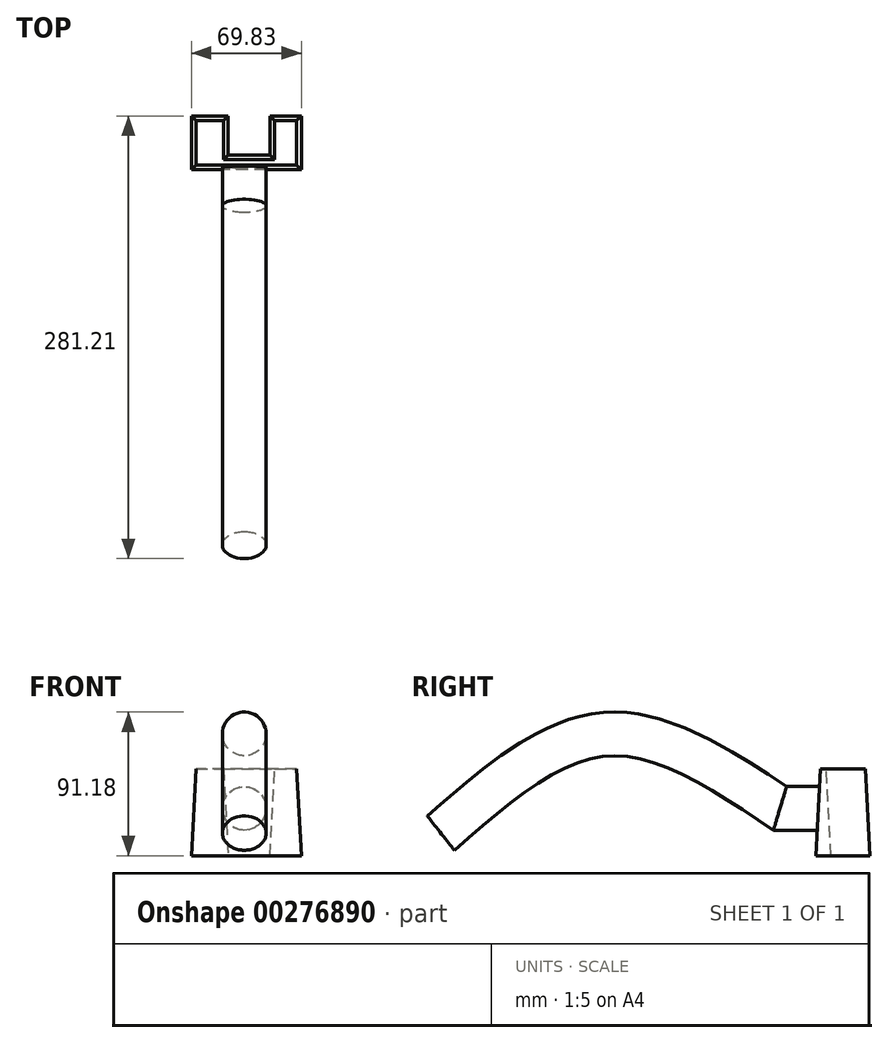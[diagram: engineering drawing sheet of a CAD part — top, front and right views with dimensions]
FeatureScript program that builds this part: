
annotation { "Feature Type Name" : "Feature", "Feature Type Description" : "" }
export const myFeature = defineFeature(function(context is Context, id is Id, definition is map)
    precondition{}
    {
        {
            var Q0;
            Q0=qCreatedBy(makeId("Top.planeOp"),FACE);
            var sketch = newSketch(context, id + "F0", { "sketchPlane" : qUnion([Q0])});
            skLineSegment(sketch, "E0.bottom", {"start": v(0, 0) * mm, "end": v(69.83, 0) * mm});
            skLineSegment(sketch, "E0.top", {"start": v(0, 34.25) * mm, "end": v(23.28, 34.25) * mm});
            skLineSegment(sketch, "E0.left", {"start": v(0, 0) * mm, "end": v(0, 34.25) * mm});
            skLineSegment(sketch, "E0.right", {"start": v(69.83, 0) * mm, "end": v(69.83, 34.25) * mm});
            skLineSegment(sketch, "E1.top", {"start": v(23.28, 9.39) * mm, "end": v(49.99, 9.39) * mm});
            skLineSegment(sketch, "E1.left", {"start": v(23.28, 34.25) * mm, "end": v(23.28, 9.39) * mm});
            skLineSegment(sketch, "E1.right", {"start": v(49.99, 34.25) * mm, "end": v(49.99, 9.39) * mm});
            skLineSegment(sketch, "E2.trimOffspring", {"start": v(49.99, 34.25) * mm, "end": v(69.83, 34.25) * mm});
            skSolve(sketch);
        }
        {
            var Q0;
            Q0=makeQuery(id+"F0.imprint","IMPRINT",FACE,{"disambiguationData":[TD([[makeQuery(id+"F0.imprint","IMPRINT",EDGE,{"derivedFrom":sQuery(id+"F0.wireOp",EDGE,"E0.bottom")}),1.0]])]});
            extrude(context, id + "F1", {"entities" : qUnion([Q0]), "depth" : 55.12 * mm, "hasDraft" : true, "draftAngle" : 3 * degree, "draftPullDirection" : true});
        }
        {
            var Q0;
            Q0=makeQuery(id+"F1.opExtrude","SWEPT_FACE",FACE,{"disambiguationData":[OSD([sQuery(id+"F0.wireOp",EDGE,"E0.bottom")])]});
            var sketch = newSketch(context, id + "F2", { "sketchPlane" : qUnion([Q0])});
            skCircle(sketch, "E3", {"center": v(33.6, 30.06) * mm, "radius": 13.87 * mm});
            skSolve(sketch);
        }
        {
            var Q0;
            Q0=qCreatedBy(makeId("Right.planeOp"),FACE);
            var sketch = newSketch(context, id + "F3", { "sketchPlane" : qUnion([Q0])});
            skLineSegment(sketch, "E4", {"start": v(3.44, 29.76) * mm, "end": v(-23.01, 29.76) * mm});
            skPoint(sketch, "E5.3.internal.orphan", {"position": v(-71.94, 29.76) * mm});
            skFitSpline(sketch, "E6", {"points": [v(-23.01, 29.76) * mm, v(-133.16, 76.9) * mm, v(-238.22, 14.1) * mm], "startDerivative": vector(-224.58, 149.42) * mm, "endDerivative": vector(-205.88, -180.13) * mm});
            skSolve(sketch);
        }
        {
            var Q0;
            Q0=makeQuery(id+"F2.imprint","IMPRINT",FACE,{"disambiguationData":[TD([[makeQuery(id+"F2.imprint","IMPRINT",EDGE,{"derivedFrom":sQuery(id+"F2.wireOp",EDGE,"E3")}),1.0]])]});
            var Q1;
            Q1=sQuery(id+"F3.wireOp",EDGE,"E6");
            var Q2;
            Q2=sQuery(id+"F3.wireOp",EDGE,"E4");
            sweep(context, id + "F4", {"operationType" : NewBodyOperationType.ADD, "profiles" : qUnion([Q0]), "path" : qUnion([Q1, Q2])});
        }
    });
